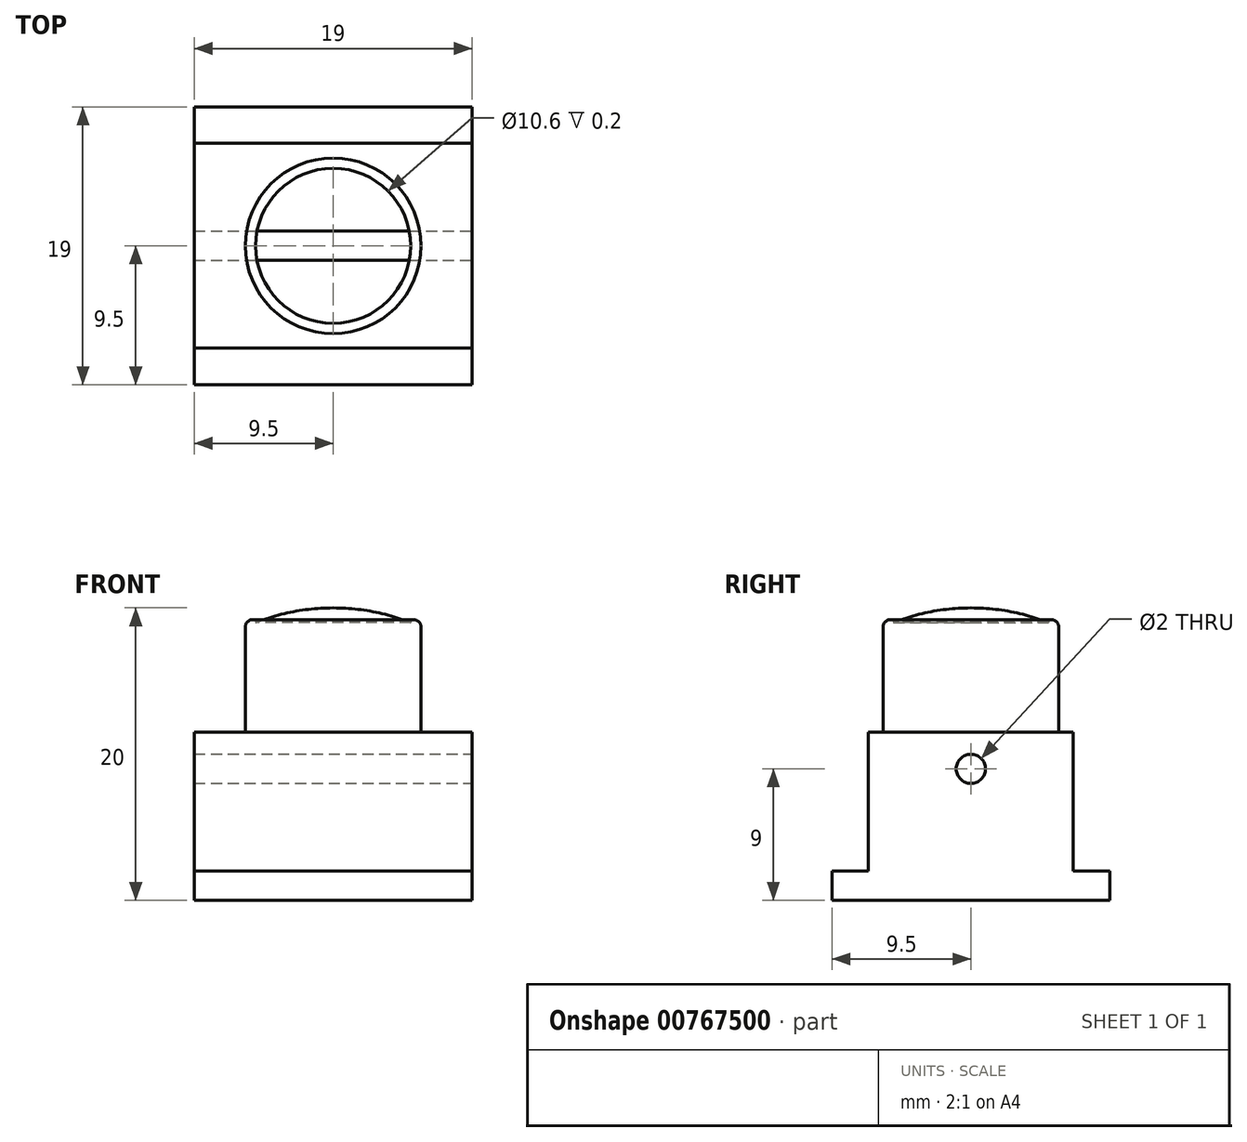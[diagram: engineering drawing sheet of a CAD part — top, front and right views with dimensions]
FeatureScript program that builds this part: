
annotation { "Feature Type Name" : "Feature", "Feature Type Description" : "" }
export const myFeature = defineFeature(function(context is Context, id is Id, definition is map)
    precondition{}
    {
        {
            var Q0;
            Q0=qCreatedBy(makeId("Top.planeOp"),FACE);
            var sketch = newSketch(context, id + "F0", { "sketchPlane" : qUnion([Q0])});
            skLineSegment(sketch, "E0.bottom", {"start": v(9.5, 9.5) * mm, "end": v(-9.5, 9.5) * mm});
            skLineSegment(sketch, "E0.top", {"start": v(9.5, -9.5) * mm, "end": v(-9.5, -9.5) * mm});
            skLineSegment(sketch, "E0.left", {"start": v(9.5, 9.5) * mm, "end": v(9.5, -9.5) * mm});
            skLineSegment(sketch, "E0.right", {"start": v(-9.5, 9.5) * mm, "end": v(-9.5, -9.5) * mm});
            skPoint(sketch, "E0.middle", {"position": v(0, 0) * mm});
            skSolve(sketch);
        }
        {
            var Q0;
            Q0=qCreatedBy(makeId("Top.planeOp"),FACE);
            var sketch = newSketch(context, id + "F1", { "sketchPlane" : qUnion([Q0])});
            skCircle(sketch, "E1", {"center": v(0, 0) * mm, "radius": 6 * mm});
            skSolve(sketch);
        }
        {
            var Q0;
            Q0=qCreatedBy(makeId("Top.planeOp"),FACE);
            var sketch = newSketch(context, id + "F2", { "sketchPlane" : qUnion([Q0])});
            skLineSegment(sketch, "E2.bottom", {"start": v(-9.5, 7) * mm, "end": v(9.5, 7) * mm});
            skLineSegment(sketch, "E2.top", {"start": v(-9.5, -7) * mm, "end": v(9.5, -7) * mm});
            skLineSegment(sketch, "E2.left", {"start": v(-9.5, 7) * mm, "end": v(-9.5, -7) * mm});
            skLineSegment(sketch, "E2.right", {"start": v(9.5, 7) * mm, "end": v(9.5, -7) * mm});
            skPoint(sketch, "E2.middle", {"position": v(0, 0) * mm});
            skSolve(sketch);
        }
        {
            var Q0;
            Q0=makeQuery(id+"F0.imprint","IMPRINT",FACE,{"disambiguationData":[TD([[makeQuery(id+"F0.imprint","IMPRINT",EDGE,{"derivedFrom":sQuery(id+"F0.wireOp",EDGE,"E0.bottom")}),1.0]])]});
            extrude(context, id + "F3", {"entities" : qUnion([Q0]), "depth" : 2 * mm, "offsetDistance" : 25 * mm});
        }
        {
            var Q0;
            Q0 = qSketchRegion(id + "F2", true);
            extrude(context, id + "F4", {"entities" : qUnion([Q0]), "operationType" : NewBodyOperationType.ADD, "depth" : 11.5 * mm, "offsetDistance" : 25 * mm, "hasSecondDirection" : true, "secondDirectionOppositeDirection" : false, "secondDirectionDepth" : 2 * mm});
        }
        {
            var Q0;
            Q0 = qSketchRegion(id + "F1", true);
            extrude(context, id + "F5", {"entities" : qUnion([Q0]), "operationType" : NewBodyOperationType.ADD, "depth" : 19 * mm, "offsetDistance" : 25 * mm, "hasSecondDirection" : true, "secondDirectionOppositeDirection" : false, "secondDirectionDepth" : 11.5 * mm});
        }
        {
            var Q0;
            Q0=qCreatedBy(makeId("Right.planeOp"),FACE);
            var sketch = newSketch(context, id + "F6", { "sketchPlane" : qUnion([Q0])});
            skLineSegment(sketch, "E3", {"start": v(0, 0) * mm, "end": v(0, 9) * mm, "construction": true});
            skCircle(sketch, "E4", {"center": v(0, 9) * mm, "radius": 1 * mm});
            skSolve(sketch);
        }
        {
            var Q0;
            Q0 = qSketchRegion(id + "F6", true);
            extrude(context, id + "F7", {"entities" : qUnion([Q0]), "operationType" : NewBodyOperationType.REMOVE, "oppositeDirection" : true, "depth" : 25 * mm, "offsetDistance" : 25 * mm, "hasSecondDirection" : true, "secondDirectionOppositeDirection" : false, "secondDirectionDepth" : 25 * mm});
        }
        {
            var Q0;
            Q0=makeQuery(id+"F5.opExtrude","CAP_FACE",FACE,{"disambiguationData":[OSD([sQuery(id+"F1.wireOp",EDGE,"E1")])],"isStart":false});
            var sketch = newSketch(context, id + "F8", { "sketchPlane" : qUnion([Q0])});
            skCircle(sketch, "E5.0", {"center": v(0, 0) * mm, "radius": 5.3 * mm});
            skSolve(sketch);
        }
        {
            var Q0;
            Q0 = qSketchRegion(id + "F8", true);
            extrude(context, id + "F9", {"entities" : qUnion([Q0]), "operationType" : NewBodyOperationType.ADD, "depth" : 1 * mm, "offsetDistance" : 25 * mm});
        }
        {
            var Q0;
            Q0=makeQuery(id+"F9.opExtrude","CAP_EDGE",EDGE,{"disambiguationData":[OSD([sQuery(id+"F8.wireOp",EDGE,"E5.0")])],"isStart":false});
            fillet(context, id + "F10", {"entities" : qUnion([Q0]), "radius" : 14.5 * mm, "tangentPropagation" : true, "allowEdgeOverflow" : false});
        }
        {
            var Q0;
            Q0=makeQuery(id+"F5.opExtrude","CAP_FACE",FACE,{"disambiguationData":[OSD([sQuery(id+"F1.wireOp",EDGE,"E1")])],"isStart":false});
            extrude(context, id + "F11", {"entities" : qUnion([Q0]), "operationType" : NewBodyOperationType.ADD, "depth" : .2 * mm, "offsetDistance" : 25 * mm});
        }
        {
            var Q0;
            Q0=makeQuery(id+"F11.opExtrude","CAP_EDGE",EDGE,{"disambiguationData":[OSD([sQuery(id+"F1.wireOp",EDGE,"E1")])],"isStart":false});
            fillet(context, id + "F12", {"entities" : qUnion([Q0]), "radius" : .5 * mm, "tangentPropagation" : true, "allowEdgeOverflow" : false});
        }
    });
